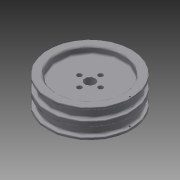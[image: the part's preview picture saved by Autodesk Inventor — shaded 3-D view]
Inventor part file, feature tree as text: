
AUTODESK INVENTOR PART (.ipt)
format: ipt  version: 2014 SP2 (Build 180246200, 246)  size: 303,104 bytes
history: native  units: in
note: dims shown in document units (in); Inventor stores cm internally (conversion verified against a paired STEP export)
features: sketch x7, extrude x5, fillet x4, revolve x1, mirror x1
ambient origin geometry x8: Origin, YZ Plane, XZ Plane, XY Plane, X Axis, Y Axis, Z Axis, Center Point
bodies: Solid1 (feature_tree)
feature tree (18):
  sketch  "Sketch1"  dims[d0=2.5in d1=0.5in]
  revolve  "Revolution1"  [1 undecoded]
  extrude  "Extrusion1"  Depth=0.075in
  mirror  "Mirror1"
  extrude  "Extrusion2"  Depth=0.158in
  fillet  "Fillet2"  [1 undecoded]
  extrude  "Extrusion3"  Depth=0.146in
  fillet  "Fillet3"  Radius=1.5748in
  fillet  "Fillet4"  Radius=1.0in
  extrude  "Extrusion4"  Depth=0.2in TaperAngle=0.0deg
  extrude  "Extrusion5"  Depth=0.05in
  fillet  "Fillet5"  Radius=2.0in
  sketch  "Sketch2"  dims[d2=0.075in d5=0.075in]
  sketch  "Sketch3"  dims[d6=1.25in d7=0.158in d8=90.0deg]
  sketch  "Sketch4"  dims[d10=0.315in d11=0.146in d12=1.5748in d14=360.0deg d16=1.0in d17=0.0in]
  sketch  "Sketch5"  dims[d18=2.0in d19=0.2in d20=0.0in]
  sketch  "Sketch6"  dims[d21=0.05in d22=1.9in d23=2.0in]
  sketch  "Sketch7"  dims[d24=0.2in d25=0.0in d26=0.05in d27=0.02in d28=0.05in d29=0.3in d30=0.0in d31=0.3in d32=0.0in d33=0.05in]
note: 2 required parameter values undecoded (feature->parameter linkage not recoverable at this tier; creation-order binding heuristic only, values carry confidence <= 0.55)